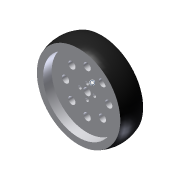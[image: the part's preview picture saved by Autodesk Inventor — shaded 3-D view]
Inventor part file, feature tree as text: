
AUTODESK INVENTOR PART (.ipt)
format: ipt  version: 2013 (Build 170138000, 138)  size: 158,208 bytes
history: native  units: in
note: dims shown in document units (in); Inventor stores cm internally (conversion verified against a paired STEP export)
features: other x1, imported_body x1, plane x1
ambient origin geometry x8: Origin, YZ Plane, XZ Plane, XY Plane, X Axis, Y Axis, Z Axis, Center Point
feature tree (3):
  other  "WHEEL_101MM_4-IN_2011"
  imported_body  "Base1"
  plane  "Work Plane1"
